FCSTD DOCUMENT  (FreeCAD 0.20R26155 (Git))
Label: 01x05_PCBsidemount_pads
License: All rights reserved
LicenseURL: http://en.wikipedia.org/wiki/All_rights_reserved
objects: Sketcher::SketchObject×1
note: 1 computed .brp shape members not serialized (recipe doc carries the construction recipe); baked Part::Feature solids carry a one-line shape summary decoded from their .brp

FEATURE [Sketcher::SketchObject] Sketch  label="Pads_TH_SMD"
  FullyConstrained = true
  sketch-geometry (25):
    g0: LineSegment StartX=0 StartY=0 StartZ=0 EndX=1 EndY=0 EndZ=0
    g1: LineSegment StartX=1 StartY=0 StartZ=0 EndX=1 EndY=4 EndZ=0
    g2: LineSegment StartX=1 StartY=4 StartZ=0 EndX=0 EndY=4 EndZ=0
    g3: LineSegment StartX=0 StartY=4 StartZ=0 EndX=0 EndY=0 EndZ=0
    g4: LineSegment StartX=0.5 StartY=4 StartZ=0 EndX=0.5 EndY=0 EndZ=0
    g5: LineSegment StartX=2.54 StartY=0 StartZ=0 EndX=3.54 EndY=0 EndZ=0
    g6: LineSegment StartX=3.54 StartY=0 StartZ=0 EndX=3.54 EndY=4 EndZ=0
    g7: LineSegment StartX=3.54 StartY=4 StartZ=0 EndX=2.54 EndY=4 EndZ=0
    g8: LineSegment StartX=2.54 StartY=4 StartZ=0 EndX=2.54 EndY=0 EndZ=0
    g9: LineSegment StartX=3.04 StartY=4 StartZ=0 EndX=3.04 EndY=0 EndZ=0
    g10: LineSegment StartX=5.08 StartY=0 StartZ=0 EndX=6.08 EndY=0 EndZ=0
    g11: LineSegment StartX=6.08 StartY=0 StartZ=0 EndX=6.08 EndY=4 EndZ=0
    g12: LineSegment StartX=6.08 StartY=4 StartZ=0 EndX=5.08 EndY=4 EndZ=0
    g13: LineSegment StartX=5.08 StartY=4 StartZ=0 EndX=5.08 EndY=0 EndZ=0
    g14: LineSegment StartX=5.58 StartY=4 StartZ=0 EndX=5.58 EndY=0 EndZ=0
    g15: LineSegment StartX=7.62 StartY=0 StartZ=0 EndX=8.62 EndY=0 EndZ=0
    g16: LineSegment StartX=8.62 StartY=0 StartZ=0 EndX=8.62 EndY=4 EndZ=0
    g17: LineSegment StartX=8.62 StartY=4 StartZ=0 EndX=7.62 EndY=4 EndZ=0
    g18: LineSegment StartX=7.62 StartY=4 StartZ=0 EndX=7.62 EndY=0 EndZ=0
    g19: LineSegment StartX=8.12 StartY=4 StartZ=0 EndX=8.12 EndY=0 EndZ=0
    g20: LineSegment StartX=10.16 StartY=0 StartZ=0 EndX=11.16 EndY=0 EndZ=0
    g21: LineSegment StartX=11.16 StartY=0 StartZ=0 EndX=11.16 EndY=4 EndZ=0
    g22: LineSegment StartX=11.16 StartY=4 StartZ=0 EndX=10.16 EndY=4 EndZ=0
    g23: LineSegment StartX=10.16 StartY=4 StartZ=0 EndX=10.16 EndY=0 EndZ=0
    g24: LineSegment StartX=10.66 StartY=4 StartZ=0 EndX=10.66 EndY=0 EndZ=0
  constraints (74):
    c: Coincident(g0,g1)
    c: Coincident(g1,g2)
    c: Coincident(g2,g3)
    c: Coincident(g3,g0)
    c: Horizontal(g0)
    c: Horizontal(g2)
    c: Vertical(g1)
    c: Vertical(g3)
    c: Coincident(g0,g-1)
    c: PointOnObject(g4,g2)
    c: PointOnObject(g4,g0)
    c: Symmetric(g1,g2,g4)
    c: DistanceY(g3,g3) = 4
    c: DistanceX(g2,g2) = 1
    c: Coincident(g5,g6)
    c: Coincident(g6,g7)
    c: Coincident(g7,g8)
    c: Coincident(g8,g5)
    c: Horizontal(g5)
    c: Horizontal(g7)
    c: Vertical(g6)
    c: Vertical(g8)
    c: PointOnObject(g9,g7)
    c: PointOnObject(g9,g5)
    c: Symmetric(g6,g7,g9)
    c: Equal(g3,g8) = 4
    c: Equal(g2,g7) = 1
    c: PointOnObject(g5,g-1)
    c: Coincident(g10,g11)
    c: Coincident(g11,g12)
    c: Coincident(g12,g13)
    c: Coincident(g13,g10)
    c: Horizontal(g10)
    c: Horizontal(g12)
    c: Vertical(g11)
    c: Vertical(g13)
    c: PointOnObject(g14,g12)
    c: PointOnObject(g14,g10)
    c: Symmetric(g11,g12,g14)
    c: Coincident(g15,g16)
    c: Coincident(g16,g17)
    c: Coincident(g17,g18)
    c: Coincident(g18,g15)
    c: Horizontal(g15)
    c: Horizontal(g17)
    c: Vertical(g16)
    c: Vertical(g18)
    c: PointOnObject(g19,g17)
    c: PointOnObject(g19,g15)
    c: Symmetric(g16,g17,g19)
    c: Coincident(g20,g21)
    c: Coincident(g21,g22)
    c: Coincident(g22,g23)
    c: Coincident(g23,g20)
    c: Horizontal(g20)
    c: Horizontal(g22)
    c: Vertical(g21)
    c: Vertical(g23)
    c: PointOnObject(g24,g22)
    c: PointOnObject(g24,g20)
    c: Symmetric(g21,g22,g24)
    c: Equal(g1,g11)
    c: Equal(g11,g16)
    c: Equal(g16,g21)
    c: Equal(g7,g12)
    c: Equal(g12,g17)
    c: Equal(g17,g22)
    c: PointOnObject(g10,g-1)
    c: PointOnObject(g15,g-1)
    c: PointOnObject(g20,g-1)
    c: DistanceX(g4,g9) = 2.54
    c: DistanceX(g9,g14) = 2.54
    c: DistanceX(g14,g19) = 2.54
    c: DistanceX(g19,g24) = 2.54
